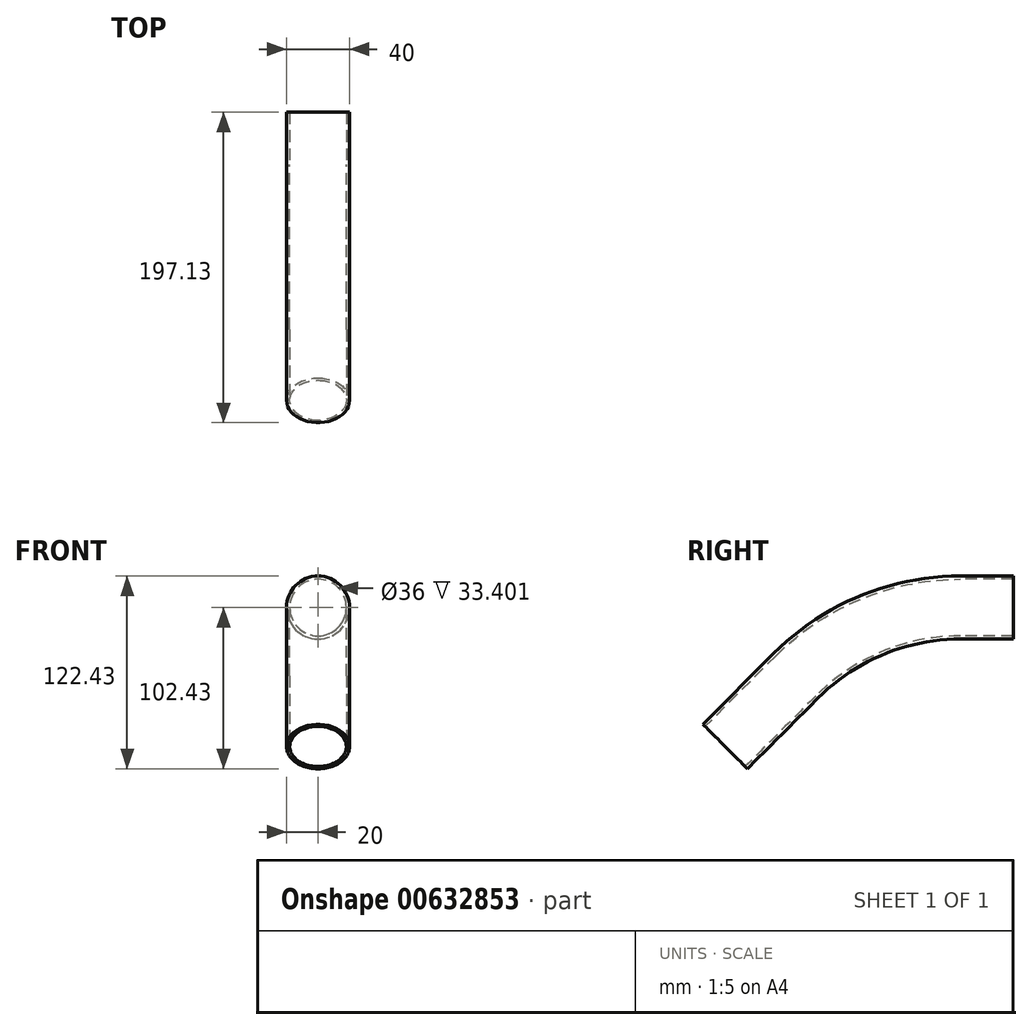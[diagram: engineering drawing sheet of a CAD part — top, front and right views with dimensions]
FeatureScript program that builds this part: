
annotation { "Feature Type Name" : "Feature", "Feature Type Description" : "" }
export const myFeature = defineFeature(function(context is Context, id is Id, definition is map)
    precondition{}
    {
        {
            var Q0;
            Q0=qCreatedBy(makeId("Front.planeOp"),FACE);
            var sketch = newSketch(context, id + "F0", { "sketchPlane" : qUnion([Q0])});
            skCircle(sketch, "E0", {"center": v(0, 0) * mm, "radius": 20 * mm});
            skCircle(sketch, "E1.0", {"center": v(0, 0) * mm, "radius": 18 * mm});
            skSolve(sketch);
        }
        {
            var Q0;
            Q0=qCreatedBy(makeId("Right.planeOp"),FACE);
            var sketch = newSketch(context, id + "F1", { "sketchPlane" : qUnion([Q0])});
            skLineSegment(sketch, "E2", {"start": v(-104.64, -43.34) * mm, "end": v(-149.6, -88.3) * mm});
            skLineSegment(sketch, "E3", {"start": v(0, 0) * mm, "end": v(0, -147.99) * mm, "construction": true});
            skArc(sketch, "E4", {"start": v(0, 0) * mm, "mid": v(-56.63, -11.26) * mm, "end": v(-104.64, -43.34) * mm});
            skSolve(sketch);
        }
        {
            var Q0;
            Q0=makeQuery(id+"F0.imprint","IMPRINT",FACE,{"disambiguationData":[TD([[makeQuery(id+"F0.imprint","IMPRINT",EDGE,{"derivedFrom":sQuery(id+"F0.wireOp",EDGE,"E0")}),1.0]])]});
            var Q1;
            Q1=sQuery(id+"F0.wireOp",EDGE,"E0");
            var Q2;
            Q2 = qBodyType(qCreatedBy(id + "F1" ,EDGE), BodyType.WIRE);
            sweep(context, id + "F2", {"profiles" : qUnion([Q0]), "surfaceProfiles" : qUnion([Q1]), "path" : qUnion([Q2])});
        }
        {
            var Q0;
            Q0=makeQuery(id+"F2.opSweep","CAP_FACE",FACE,{"disambiguationData":[OSD([sQuery(id+"F0.wireOp",EDGE,"E0"),sQuery(id+"F0.wireOp",EDGE,"E1.0"),sQuery(id+"F1.wireOp",VERTEX,"E2.start")])],"isStart":true});
            extrude(context, id + "F3", {"entities" : qUnion([Q0]), "operationType" : NewBodyOperationType.ADD, "depth" : 33.4 * mm, "offsetDistance" : 25 * mm});
        }
    });
